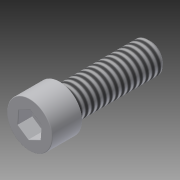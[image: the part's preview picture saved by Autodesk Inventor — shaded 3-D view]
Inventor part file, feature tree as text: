
AUTODESK INVENTOR PART (.ipt)
format: ipt  version: 2014 (Build 180170000, 170)  size: 131,072 bytes
history: native  units: in
note: dims shown in document units (in); Inventor stores cm internally (conversion verified against a paired STEP export)
features: extrude x3, fillet x3, sketch x3, projected_geometry x2, thread x1, chamfer x1
ambient origin geometry x8: Origin, YZ Plane, XZ Plane, XY Plane, X Axis, Y Axis, Z Axis, Center Point
bodies: Solid1 (feature_tree)
feature tree (13):
  extrude  "Extrusion1"  TaperAngle=0.0deg  [1 undecoded]
  extrude  "Extrusion2"  Depth=1.0in TaperAngle=0.0deg
  extrude  "Extrusion3"  Depth=0.005in
  thread  "Thread2"  [1 undecoded]
  chamfer  "Chamfer1"  Distance=0.005in
  fillet  "Fillet1"  [1 undecoded]
  fillet  "Fillet2"  [1 undecoded]
  fillet  "Fillet3"  [1 undecoded]
  sketch  "Sketch1"  dims[d2=0.0in d5=0.0in]
  sketch  "Sketch2"  dims[d8=0.0in d11=1.0in d12=0.0in]
  projected_geometry  "Projected Loop1"
  sketch  "Sketch3"  dims[d13=0.025in d14=0.125in d15=45.0deg d16=0.005in d17=0.005in d18=0.005in]
  projected_geometry  "Projected Loop2"
note: 5 required parameter values undecoded (feature->parameter linkage not recoverable at this tier; creation-order binding heuristic only, values carry confidence <= 0.55)
